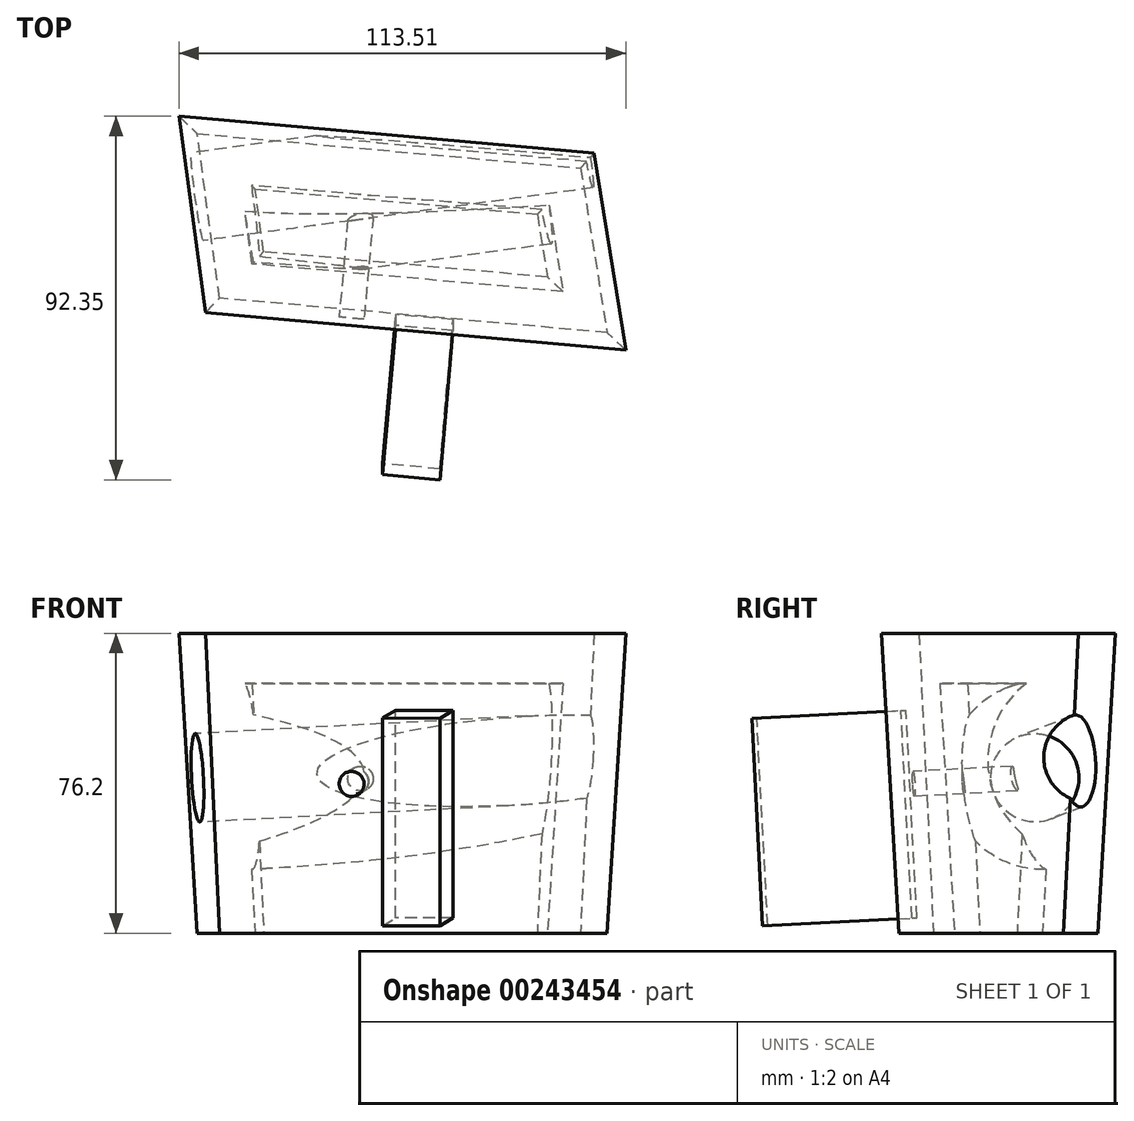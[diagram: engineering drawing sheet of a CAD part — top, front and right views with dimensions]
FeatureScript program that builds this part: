
annotation { "Feature Type Name" : "Feature", "Feature Type Description" : "" }
export const myFeature = defineFeature(function(context is Context, id is Id, definition is map)
    precondition{}
    {
        {
            var Q0;
            Q0=qCreatedBy(makeId("Top.planeOp"),FACE);
            var sketch = newSketch(context, id + "F0", { "sketchPlane" : qUnion([Q0])});
            skLineSegment(sketch, "E0", {"start": v(-97.38, 8.7) * mm, "end": v(0, 0) * mm});
            skLineSegment(sketch, "E1", {"start": v(0, 0) * mm, "end": v(6.74, -41.85) * mm});
            skLineSegment(sketch, "E2", {"start": v(6.74, -41.85) * mm, "end": v(-91.72, -33.07) * mm});
            skLineSegment(sketch, "E3", {"start": v(-91.72, -33.07) * mm, "end": v(-97.38, 8.7) * mm});
            skSolve(sketch);
        }
        {
            var Q0;
            Q0=makeQuery(id+"F0.imprint","IMPRINT",FACE,{"disambiguationData":[TD([[makeQuery(id+"F0.imprint","IMPRINT",EDGE,{"derivedFrom":sQuery(id+"F0.wireOp",EDGE,"E0")}),-1.0]])]});
            extrude(context, id + "F1", {"entities" : qUnion([Q0]), "depth" : 76.2 * mm, "hasDraft" : true, "draftAngle" : 3 * degree});
        }
        {
            var Q0;
            Q0=makeQuery(id+"F1.opExtrude","SWEPT_FACE",FACE,{"disambiguationData":[OSD([sQuery(id+"F0.wireOp",EDGE,"E3")])]});
            var sketch = newSketch(context, id + "F2", { "sketchPlane" : qUnion([Q0])});
            skCircle(sketch, "E4", {"center": v(-5.53, 44.56) * mm, "radius": 11.26 * mm});
            skSolve(sketch);
        }
        {
            var Q0;
            Q0=makeQuery(id+"F2.imprint","IMPRINT",FACE,{"disambiguationData":[TD([[makeQuery(id+"F2.imprint","IMPRINT",EDGE,{"derivedFrom":sQuery(id+"F2.wireOp",EDGE,"E4")}),1.0]])]});
            extrude(context, id + "F3", {"entities" : qUnion([Q0]), "operationType" : NewBodyOperationType.REMOVE, "oppositeDirection" : true, "depth" : 127 * mm});
        }
        {
            var Q0;
            Q0=makeQuery(id+"F1.opExtrude","CAP_FACE",FACE,{"disambiguationData":[OSD([sQuery(id+"F0.wireOp",EDGE,"E0"),sQuery(id+"F0.wireOp",EDGE,"E1"),sQuery(id+"F0.wireOp",EDGE,"E2"),sQuery(id+"F0.wireOp",EDGE,"E3")])],"isStart":true});
            shell(context, id + "F4", {"entities" : qUnion([Q0]), "thickness" : 12.7 * mm});
        }
        {
            var Q0;
            Q0=makeQuery(id+"F1.opExtrude","SWEPT_FACE",FACE,{"disambiguationData":[OSD([sQuery(id+"F0.wireOp",EDGE,"E2")])]});
            var sketch = newSketch(context, id + "F7", { "sketchPlane" : qUnion([Q0])});
            skCircle(sketch, "E5", {"center": v(-54.72, 39.88) * mm, "radius": 17.97 * mm});
            skPoint(sketch, "E5.centerSnap0", {"position": v(-90.2, 39.88) * mm});
            skSolve(sketch);
        }
        {
            var Q0;
            Q0=sQuery(id+"F7.wireOp",VERTEX,"E5.center");
            var Q1;
            Q1=makeQuery(id+"F1.opExtrude","SWEPT_BODY",BODY,{"disambiguationData":[OSD([sQuery(id+"F0.wireOp",EDGE,"E0"),sQuery(id+"F0.wireOp",EDGE,"E1"),sQuery(id+"F0.wireOp",EDGE,"E2"),sQuery(id+"F0.wireOp",EDGE,"E3")])]});
            hole(context, id + "F5", {"style" : HoleStyle.SIMPLE, "endStyle" : HoleEndStyle.THROUGH, "holeDiameter" : 6.35 * mm, "tappedDepth" : 12.7 * mm, "tapClearance" : 3, "locations" : qUnion([Q0]), "scope" : qUnion([Q1])});
        }
        {
            var Q0;
            Q0=makeQuery(id+"F1.opExtrude","SWEPT_FACE",FACE,{"disambiguationData":[OSD([sQuery(id+"F0.wireOp",EDGE,"E2")])]});
            var sketch = newSketch(context, id + "F6", { "sketchPlane" : qUnion([Q0])});
            skLineSegment(sketch, "E6.bottom", {"start": v(-28.84, 5.86) * mm, "end": v(-43.47, 5.86) * mm});
            skLineSegment(sketch, "E6.top", {"start": v(-28.84, 58.69) * mm, "end": v(-43.47, 58.69) * mm});
            skLineSegment(sketch, "E6.left", {"start": v(-28.84, 5.86) * mm, "end": v(-28.84, 58.69) * mm});
            skLineSegment(sketch, "E6.right", {"start": v(-43.47, 5.86) * mm, "end": v(-43.47, 58.69) * mm});
            skPoint(sketch, "E6.middle", {"position": v(-36.15, 32.27) * mm});
            skSolve(sketch);
        }
        {
            var Q0;
            Q0=makeQuery(id+"F6.imprint","IMPRINT",FACE,{"disambiguationData":[TD([[makeQuery(id+"F6.imprint","IMPRINT",EDGE,{"derivedFrom":sQuery(id+"F6.wireOp",EDGE,"E6.bottom")}),-1.0]])]});
            extrude(context, id + "F8", {"entities" : qUnion([Q0]), "operationType" : NewBodyOperationType.ADD, "depth" : 38.1 * mm});
        }
    });
